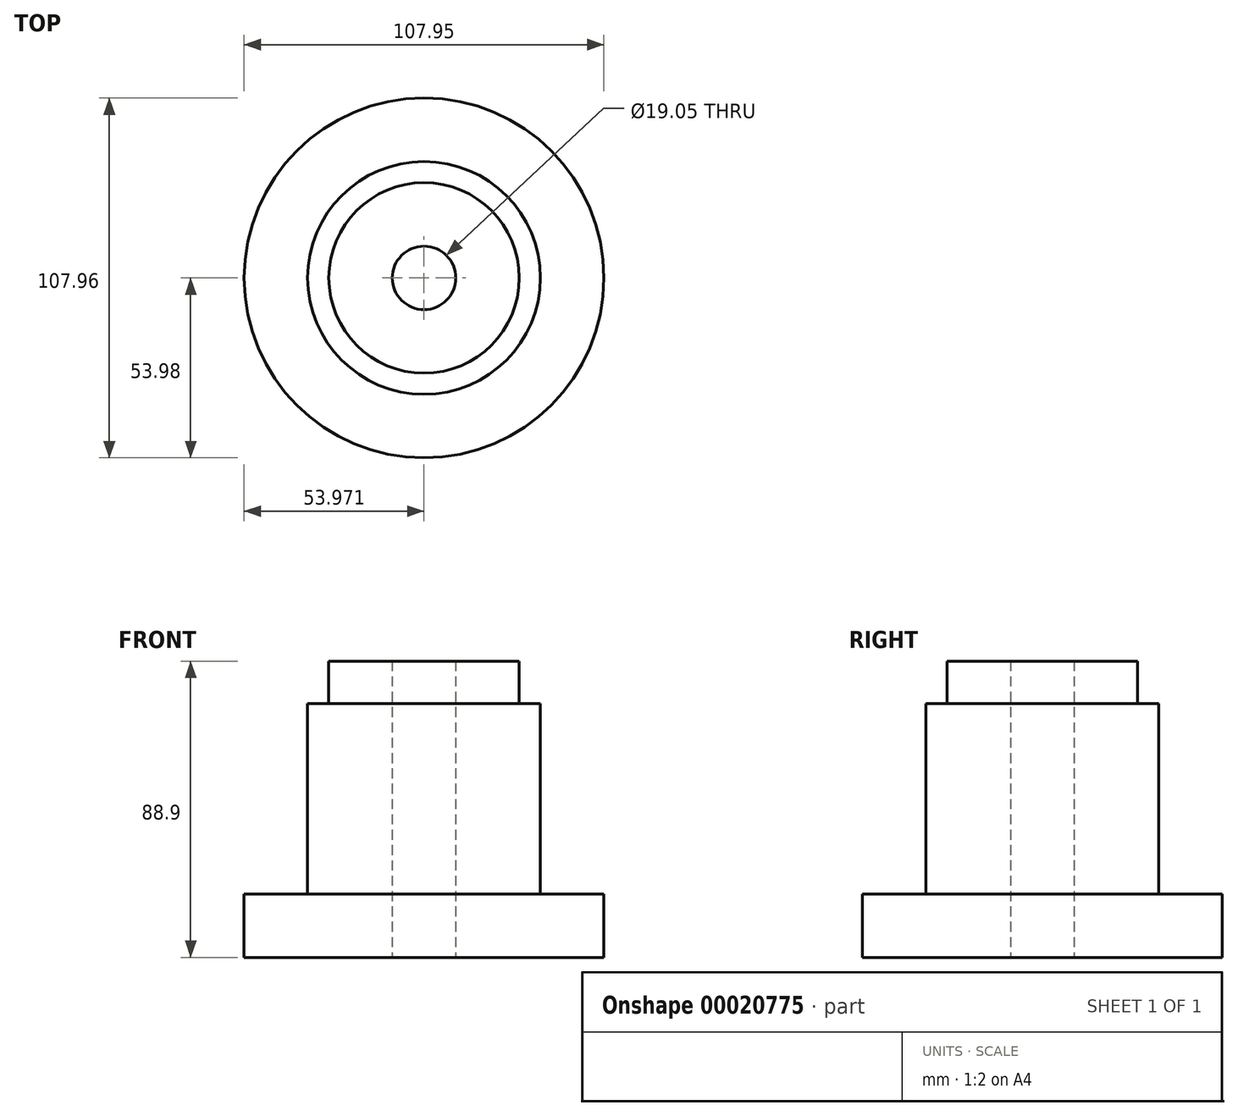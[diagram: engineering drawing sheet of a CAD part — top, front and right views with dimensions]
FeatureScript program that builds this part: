
annotation { "Feature Type Name" : "Feature", "Feature Type Description" : "" }
export const myFeature = defineFeature(function(context is Context, id is Id, definition is map)
    precondition{}
    {
        {
            var Q0;
            Q0=qCreatedBy(makeId("Front.planeOp"),FACE);
            var sketch = newSketch(context, id + "F0", { "sketchPlane" : qUnion([Q0])});
            skLineSegment(sketch, "E0", {"start": v(2.75, -41.03) * mm, "end": v(47.2, -41.03) * mm});
            skLineSegment(sketch, "E1", {"start": v(47.2, -41.03) * mm, "end": v(47.2, -21.98) * mm});
            skLineSegment(sketch, "E2", {"start": v(47.2, -21.98) * mm, "end": v(28.15, -21.98) * mm});
            skLineSegment(sketch, "E3", {"start": v(28.15, -21.98) * mm, "end": v(28.15, 35.17) * mm});
            skLineSegment(sketch, "E4", {"start": v(21.8, 35.17) * mm, "end": v(21.8, 47.87) * mm});
            skLineSegment(sketch, "E5", {"start": v(21.8, 47.87) * mm, "end": v(2.75, 47.87) * mm});
            skLineSegment(sketch, "E6", {"start": v(2.75, 47.87) * mm, "end": v(2.75, -41.03) * mm});
            skLineSegment(sketch, "E7", {"start": v(-6.78, -41.03) * mm, "end": v(-6.78, 47.09) * mm});
            skLineSegment(sketch, "E8", {"start": v(21.8, 35.17) * mm, "end": v(28.15, 35.17) * mm});
            skSolve(sketch);
        }
        {
            var Q0;
            Q0=makeQuery(id+"F0.imprint","IMPRINT",FACE,{"disambiguationData":[TD([[makeQuery(id+"F0.imprint","IMPRINT",EDGE,{"derivedFrom":sQuery(id+"F0.wireOp",EDGE,"E0")}),1.0]])]});
            var Q1;
            Q1=sQuery(id+"F0.wireOp",EDGE,"E7");
            revolve(context, id + "F1", {"entities" : qUnion([Q0]), "axis" : qUnion([Q1]), "revolveType" : RevolveType.FULL});
        }
    });
